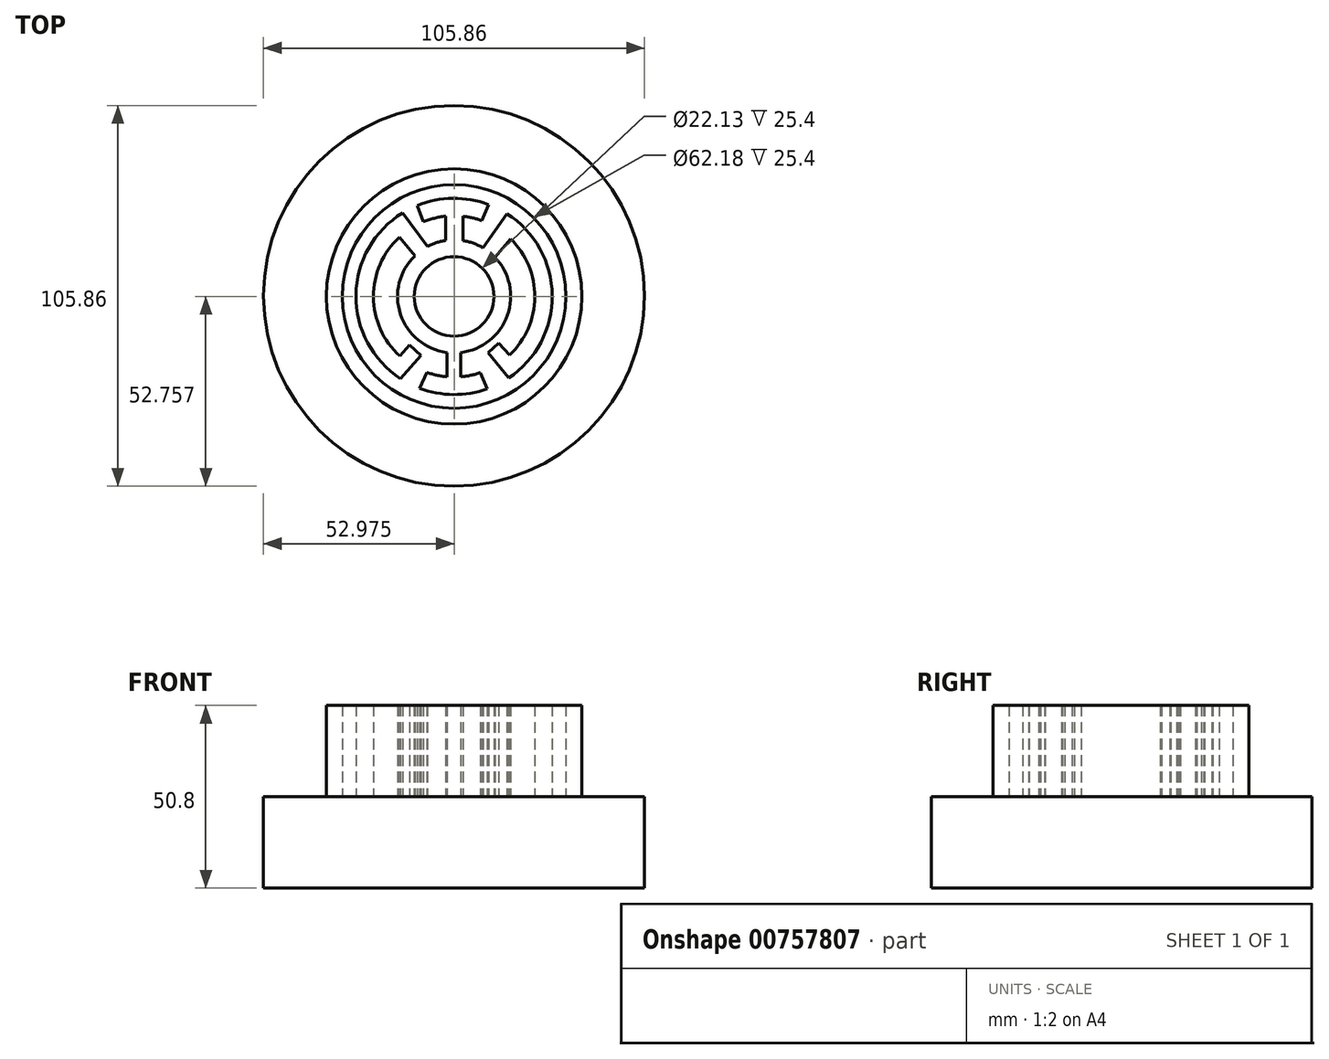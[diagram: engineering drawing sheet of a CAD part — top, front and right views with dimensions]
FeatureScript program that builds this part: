
annotation { "Feature Type Name" : "Feature", "Feature Type Description" : "" }
export const myFeature = defineFeature(function(context is Context, id is Id, definition is map)
    precondition{}
    {
        {
            var Q0;
            Q0=qCreatedBy(makeId("Top.planeOp"),FACE);
            var sketch = newSketch(context, id + "F0", { "sketchPlane" : qUnion([Q0])});
            skArc(sketch, "E0", {"start": v(39.7, 22.5) * mm, "mid": v(52.64, 32.86) * mm, "end": v(49.12, 49.05) * mm});
            skCircle(sketch, "E1", {"center": v(37.82, 38.12) * mm, "radius": 11.06 * mm});
            skCircle(sketch, "E2", {"center": v(37.82, 38.12) * mm, "radius": 35.5 * mm});
            skCircle(sketch, "E3", {"center": v(37.82, 38.12) * mm, "radius": 31.09 * mm});
            skArc(sketch, "E4", {"start": v(28.21, 12.58) * mm, "mid": v(37.62, 10.83) * mm, "end": v(47.05, 12.44) * mm});
            skArc(sketch, "E5", {"start": v(30.24, 17.01) * mm, "mid": v(32.98, 16.22) * mm, "end": v(35.8, 15.78) * mm});
            skLineSegment(sketch, "E6", {"start": v(35.43, 53.66) * mm, "end": v(35.43, 60.42) * mm});
            skLineSegment(sketch, "E7", {"start": v(40.34, 53.64) * mm, "end": v(40.34, 60.4) * mm});
            skLineSegment(sketch, "E8", {"start": v(45.46, 59.2) * mm, "end": v(47.4, 63.67) * mm});
            skLineSegment(sketch, "E9", {"start": v(29.28, 58.85) * mm, "end": v(27.58, 63.4) * mm});
            skLineSegment(sketch, "E10", {"start": v(23.52, 61.36) * mm, "end": v(30.43, 52) * mm});
            skLineSegment(sketch, "E11", {"start": v(45.83, 51.65) * mm, "end": v(52.5, 61.13) * mm});
            skLineSegment(sketch, "E12", {"start": v(22.59, 54.57) * mm, "end": v(26.93, 49.45) * mm});
            skLineSegment(sketch, "E13", {"start": v(49.12, 49.05) * mm, "end": v(53.55, 54.1) * mm});
            skLineSegment(sketch, "E14", {"start": v(53.28, 21.86) * mm, "end": v(50.2, 25.19) * mm});
            skLineSegment(sketch, "E15", {"start": v(50.2, 25.19) * mm, "end": v(47.28, 22.49) * mm});
            skLineSegment(sketch, "E16", {"start": v(22.71, 21.55) * mm, "end": v(25.44, 24.57) * mm});
            skLineSegment(sketch, "E17", {"start": v(25.44, 24.57) * mm, "end": v(28.66, 21.66) * mm});
            skLineSegment(sketch, "E18", {"start": v(35.8, 15.78) * mm, "end": v(35.8, 22.52) * mm});
            skLineSegment(sketch, "E19", {"start": v(39.7, 15.77) * mm, "end": v(39.7, 22.5) * mm});
            skLineSegment(sketch, "E20", {"start": v(28.66, 21.66) * mm, "end": v(22.9, 15.27) * mm});
            skLineSegment(sketch, "E21", {"start": v(47.28, 22.49) * mm, "end": v(52.98, 15.42) * mm});
            skLineSegment(sketch, "E22", {"start": v(45.16, 16.92) * mm, "end": v(47.05, 12.44) * mm});
            skLineSegment(sketch, "E23", {"start": v(30.24, 17.01) * mm, "end": v(28.21, 12.58) * mm});
            skArc(sketch, "E24.trimOffspring", {"start": v(39.7, 15.77) * mm, "mid": v(42.46, 16.17) * mm, "end": v(45.16, 16.92) * mm});
            skArc(sketch, "E25.trimOffspring", {"start": v(53.28, 21.86) * mm, "mid": v(60.25, 37.93) * mm, "end": v(53.55, 54.1) * mm});
            skArc(sketch, "E26.trimOffspring", {"start": v(52.98, 15.42) * mm, "mid": v(65.11, 38.4) * mm, "end": v(52.5, 61.13) * mm});
            skArc(sketch, "E27.trimOffspring", {"start": v(22.59, 54.57) * mm, "mid": v(15.4, 38.03) * mm, "end": v(22.71, 21.55) * mm});
            skArc(sketch, "E28.trimOffspring", {"start": v(23.52, 61.36) * mm, "mid": v(10.54, 38.49) * mm, "end": v(22.9, 15.27) * mm});
            skArc(sketch, "E29.trimOffspring", {"start": v(35.43, 53.66) * mm, "mid": v(32.86, 53.04) * mm, "end": v(30.43, 52) * mm});
            skArc(sketch, "E30.trimOffspring", {"start": v(26.93, 49.45) * mm, "mid": v(22.9, 33.2) * mm, "end": v(35.8, 22.52) * mm});
            skArc(sketch, "E31.trimOffspring", {"start": v(35.43, 60.42) * mm, "mid": v(32.3, 59.85) * mm, "end": v(29.28, 58.85) * mm});
            skArc(sketch, "E32.trimOffspring", {"start": v(45.46, 59.2) * mm, "mid": v(42.94, 59.96) * mm, "end": v(40.34, 60.4) * mm});
            skArc(sketch, "E33.trimOffspring", {"start": v(45.83, 51.65) * mm, "mid": v(43.18, 52.9) * mm, "end": v(40.34, 53.64) * mm});
            skArc(sketch, "E34.trimOffspring", {"start": v(47.4, 63.67) * mm, "mid": v(37.47, 65.4) * mm, "end": v(27.58, 63.4) * mm});
            skSolve(sketch);
        }
        {
            var Q0;
            Q0=qCreatedBy(makeId("Top.planeOp"),FACE);
            var sketch = newSketch(context, id + "F1", { "sketchPlane" : qUnion([Q0])});
            skCircle(sketch, "E35", {"center": v(37.78, 38.3) * mm, "radius": 52.93 * mm});
            skSolve(sketch);
        }
        {
            var Q0;
            Q0 = qSketchRegion(id + "F1", true);
            extrude(context, id + "F2", {"entities" : qUnion([Q0]), "oppositeDirection" : true, "depth" : 25.4 * mm, "offsetDistance" : 25.4 * mm});
        }
        {
            var Q0;
            Q0=makeQuery(id+"F0.imprint","IMPRINT",FACE,{"disambiguationData":[TD([[makeQuery(id+"F0.imprint","IMPRINT",EDGE,{"derivedFrom":sQuery(id+"F0.wireOp",EDGE,"E0")}),1.0]])]});
            var Q1;
            Q1=makeQuery(id+"F0.imprint","IMPRINT",FACE,{"disambiguationData":[TD([[makeQuery(id+"F0.imprint","IMPRINT",EDGE,{"derivedFrom":sQuery(id+"F0.wireOp",EDGE,"E2")}),1.0]])]});
            extrude(context, id + "F3", {"entities" : qUnion([Q0, Q1]), "operationType" : NewBodyOperationType.ADD, "depth" : 25.4 * mm, "offsetDistance" : 25.4 * mm});
        }
    });
